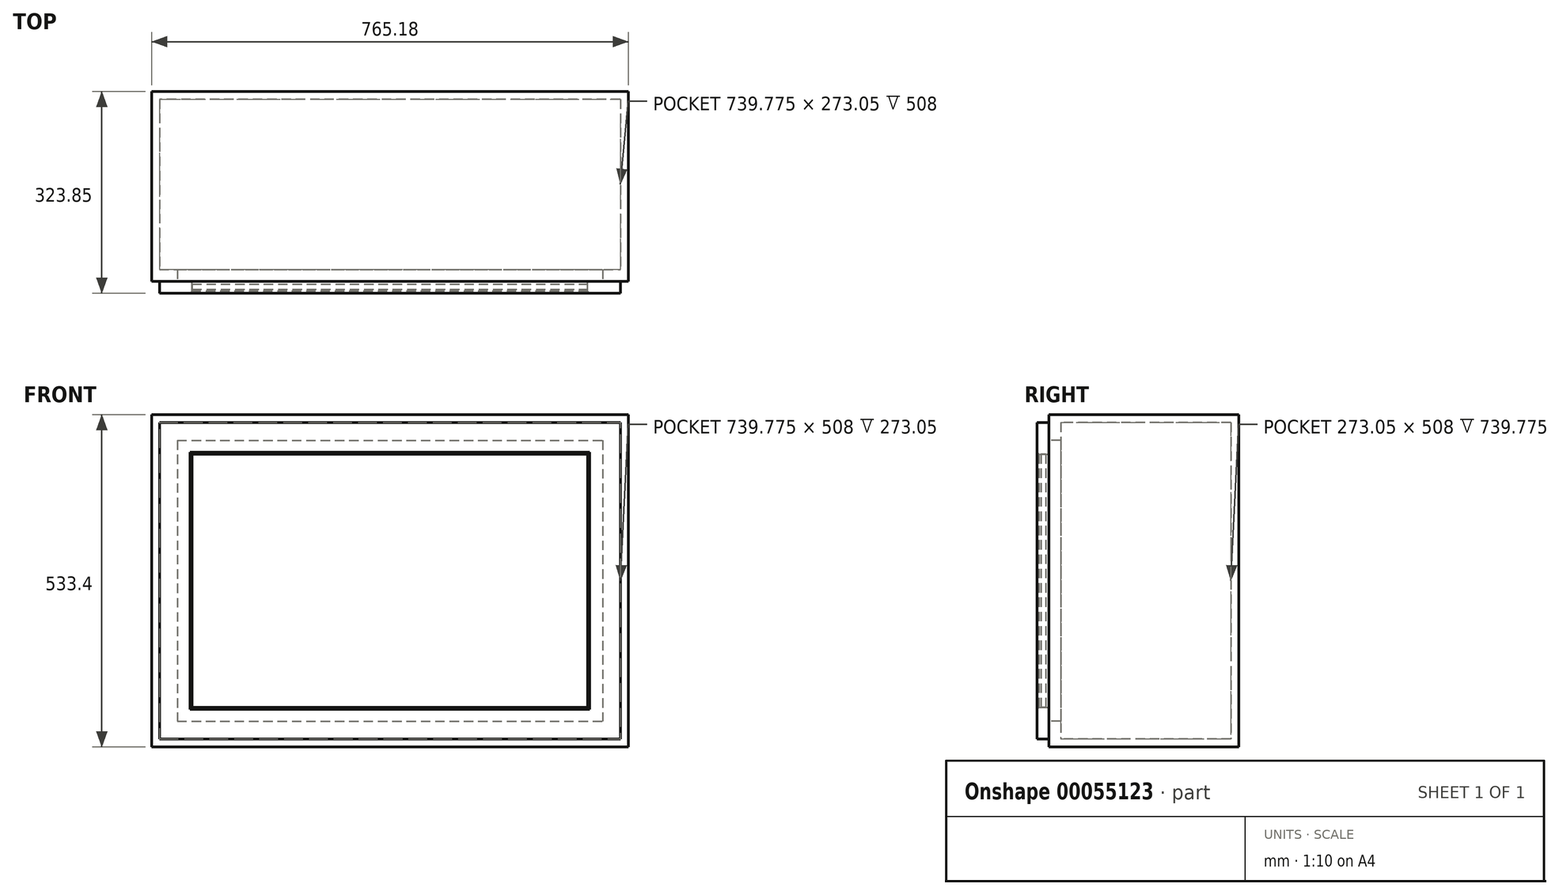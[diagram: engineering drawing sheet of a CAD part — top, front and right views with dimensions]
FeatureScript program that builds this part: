
annotation { "Feature Type Name" : "Feature", "Feature Type Description" : "" }
export const myFeature = defineFeature(function(context is Context, id is Id, definition is map)
    precondition{}
    {
        {
            var Q0;
            Q0=qCreatedBy(makeId("Top.planeOp"),FACE);
            var sketch = newSketch(context, id + "F0", { "sketchPlane" : qUnion([Q0])});
            skLineSegment(sketch, "E0.rect.bottom", {"start": v(382.59, 152.4) * mm, "end": v(-382.59, 152.4) * mm});
            skLineSegment(sketch, "E0.rect.top", {"start": v(382.59, -152.4) * mm, "end": v(-382.59, -152.4) * mm});
            skLineSegment(sketch, "E0.rect.left", {"start": v(382.59, 152.4) * mm, "end": v(382.59, -152.4) * mm});
            skLineSegment(sketch, "E0.rect.right", {"start": v(-382.59, 152.4) * mm, "end": v(-382.59, -152.4) * mm});
            skPoint(sketch, "E0.rect.middle", {"position": v(0, 0) * mm});
            skSolve(sketch);
        }
        {
            var Q0;
            Q0=qSketchRegion(id+"F0",true);
            extrude(context, id + "F1", {"entities" : qUnion([Q0]), "depth" : 533.4 * mm});
        }
        {
            var Q0;
            Q0=makeQuery(id+"F1.opExtrude","SWEPT_FACE",FACE,{"disambiguationData":[OSD([sQuery(id+"F0.wireOp",EDGE,"E0.rect.top")])]});
            shell(context, id + "F2", {"entities" : qUnion([Q0]), "thickness" : 12.7 * mm});
        }
        {
            var Q0;
            Q0=makeQuery(id+"F1.opExtrude","SWEPT_FACE",FACE,{"disambiguationData":[OSD([sQuery(id+"F0.wireOp",EDGE,"E0.rect.top")])]});
            var sketch = newSketch(context, id + "F3", { "sketchPlane" : qUnion([Q0])});
            skLineSegment(sketch, "E1", {"start": v(-382.59, 0) * mm, "end": v(382.59, 533.4) * mm, "construction": true});
            skLineSegment(sketch, "E2.rect.bottom", {"start": v(-317.5, 469.9) * mm, "end": v(317.5, 469.9) * mm});
            skLineSegment(sketch, "E2.rect.top", {"start": v(-317.5, 63.5) * mm, "end": v(317.5, 63.5) * mm});
            skLineSegment(sketch, "E2.rect.left", {"start": v(-317.5, 469.9) * mm, "end": v(-317.5, 63.5) * mm});
            skLineSegment(sketch, "E2.rect.right", {"start": v(317.5, 469.9) * mm, "end": v(317.5, 63.5) * mm});
            skPoint(sketch, "E2.rect.middle", {"position": v(0, 266.7) * mm});
            skLineSegment(sketch, "E3.rect.bottom", {"start": v(-341.31, 492.13) * mm, "end": v(341.31, 492.13) * mm});
            skLineSegment(sketch, "E3.rect.top", {"start": v(-341.31, 41.28) * mm, "end": v(341.31, 41.28) * mm});
            skLineSegment(sketch, "E3.rect.left", {"start": v(-341.31, 492.13) * mm, "end": v(-341.31, 41.28) * mm});
            skLineSegment(sketch, "E3.rect.right", {"start": v(341.31, 492.13) * mm, "end": v(341.31, 41.28) * mm});
            skLineSegment(sketch, "E4.rect.bottom", {"start": v(-382.59, 533.4) * mm, "end": v(382.59, 533.4) * mm});
            skLineSegment(sketch, "E4.rect.top", {"start": v(-382.59, 0) * mm, "end": v(382.59, 0) * mm});
            skLineSegment(sketch, "E4.rect.left", {"start": v(-382.59, 533.4) * mm, "end": v(-382.59, 0) * mm});
            skLineSegment(sketch, "E4.rect.right", {"start": v(382.59, 533.4) * mm, "end": v(382.59, 0) * mm});
            skLineSegment(sketch, "E5.rect.bottom", {"start": v(-374.65, 527.05) * mm, "end": v(374.65, 527.05) * mm});
            skLineSegment(sketch, "E5.rect.top", {"start": v(-374.65, 6.35) * mm, "end": v(374.65, 6.35) * mm});
            skLineSegment(sketch, "E5.rect.left", {"start": v(-374.65, 527.05) * mm, "end": v(-374.65, 6.35) * mm});
            skLineSegment(sketch, "E5.rect.right", {"start": v(374.65, 527.05) * mm, "end": v(374.65, 6.35) * mm});
            skSolve(sketch);
        }
        {
            var Q0;
            Q0=makeQuery(id+"F3.imprint","IMPRINT",FACE,{"disambiguationData":[TD([[makeQuery(id+"F3.imprint","IMPRINT",EDGE,{"derivedFrom":sQuery(id+"F3.wireOp",EDGE,"E4.rect.bottom")}),1.0]])]});
            var Q1;
            Q1=makeQuery(id+"F3.imprint","IMPRINT",FACE,{"disambiguationData":[TD([[makeQuery(id+"F3.imprint","IMPRINT",EDGE,{"derivedFrom":sQuery(id+"F3.wireOp",EDGE,"E5.rect.bottom")}),-1.0]])]});
            var Q2;
            Q2=makeQuery(id+"F3.imprint","IMPRINT",FACE,{"disambiguationData":[TD([[makeQuery(id+"F3.imprint","IMPRINT",EDGE,{"derivedFrom":sQuery(id+"F3.wireOp",EDGE,"E3.rect.bottom")}),1.0]])]});
            extrude(context, id + "F4", {"entities" : qUnion([Q0, Q1, Q2]), "operationType" : NewBodyOperationType.ADD, "oppositeDirection" : true, "depth" : 19.05 * mm});
        }
        {
            var Q0;
            Q0=makeQuery(id+"F3.imprint","IMPRINT",FACE,{"disambiguationData":[TD([[makeQuery(id+"F3.imprint","IMPRINT",EDGE,{"derivedFrom":sQuery(id+"F3.wireOp",EDGE,"E3.rect.bottom")}),1.0]])]});
            var Q1;
            Q1=makeQuery(id+"F3.imprint","IMPRINT",FACE,{"disambiguationData":[TD([[makeQuery(id+"F3.imprint","IMPRINT",EDGE,{"derivedFrom":sQuery(id+"F3.wireOp",EDGE,"E2.rect.bottom")}),1.0]])]});
            extrude(context, id + "F5", {"entities" : qUnion([Q0, Q1]), "operationType" : NewBodyOperationType.ADD, "depth" : 19.05 * mm});
        }
        {
            var Q0;
            Q0=makeQuery(id+"F5.opExtrude","SWEPT_FACE",FACE,{"disambiguationData":[OSD([sQuery(id+"F3.wireOp",EDGE,"E2.rect.right")])]});
            var sketch = newSketch(context, id + "F6", { "sketchPlane" : qUnion([Q0])});
            skLineSegment(sketch, "E6.bottom", {"start": v(157.16, 63.5) * mm, "end": v(165.1, 63.5) * mm});
            skLineSegment(sketch, "E6.top", {"start": v(157.16, 469.9) * mm, "end": v(165.1, 469.9) * mm});
            skLineSegment(sketch, "E6.left", {"start": v(157.16, 63.5) * mm, "end": v(157.16, 469.9) * mm});
            skLineSegment(sketch, "E6.right", {"start": v(165.1, 63.5) * mm, "end": v(165.1, 469.9) * mm});
            skSolve(sketch);
        }
        {
            var Q0;
            Q0=qSketchRegion(id+"F6",true);
            extrude(context, id + "F7", {"entities" : qUnion([Q0]), "endBound" : BoundingType.UP_TO_NEXT, "depth" : 25.4 * mm});
        }
        {
            var Q0;
            Q0=makeQuery(id+"F5.opExtrude","CAP_EDGE",EDGE,{"disambiguationData":[OSD([sQuery(id+"F3.wireOp",EDGE,"E2.rect.top")])],"isStart":false});
            var Q1;
            Q1=makeQuery(id+"F5.opExtrude","CAP_EDGE",EDGE,{"disambiguationData":[OSD([sQuery(id+"F3.wireOp",EDGE,"E2.rect.left")])],"isStart":false});
            var Q2;
            Q2=makeQuery(id+"F5.opExtrude","CAP_EDGE",EDGE,{"disambiguationData":[OSD([sQuery(id+"F3.wireOp",EDGE,"E2.rect.bottom")])],"isStart":false});
            var Q3;
            Q3=makeQuery(id+"F5.opExtrude","CAP_EDGE",EDGE,{"disambiguationData":[OSD([sQuery(id+"F3.wireOp",EDGE,"E2.rect.right")])],"isStart":false});
            chamfer(context, id + "F8", {"entities" : qUnion([Q0, Q1, Q2, Q3]), "width" : 3.17 * mm, "tangentPropagation" : true});
        }
    });
